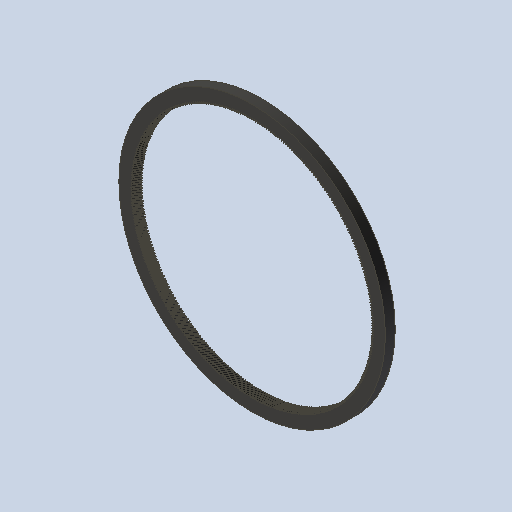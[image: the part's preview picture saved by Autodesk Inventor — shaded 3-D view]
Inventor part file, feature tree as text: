
AUTODESK INVENTOR PART (.ipt)
format: ipt  version: 2023 (Build 270158000, 158)  size: 3,780,608 bytes
history: native  units: mm (DEFAULTED — no unit token found)
features: plane x3, other x3, sketch x2, extrude x1
ambient origin geometry x8: Origin, YZ Plane, XZ Plane, XY Plane, X Axis, Y Axis, Z Axis, Center Point
bodies: Solid1 (feature_tree)
feature tree (9):
  extrude  "Extrusion1"  Depth=15.0mm TaperAngle=0.0deg
  plane  "Work Plane2"
  plane  "Work Plane8"
  plane  "Work Plane9"
  other  "Spur Gear"
  sketch  "Sketch1"  dims[d0=406.541775mm d1=15.0mm d2=0.0mm]
  sketch  "Sketch2"  dims[d3=367.141332mm d4=10.0mm d5=0.0mm d16=101.6mm d17=0.0mm d34=0.091061mm d39=0.0mm d45=0.0mm d47=101.6mm d50=0.0mm d51=0.0mm d52=101.6mm]
  other  "Srf1"
  other  "Pitch Diameter"
